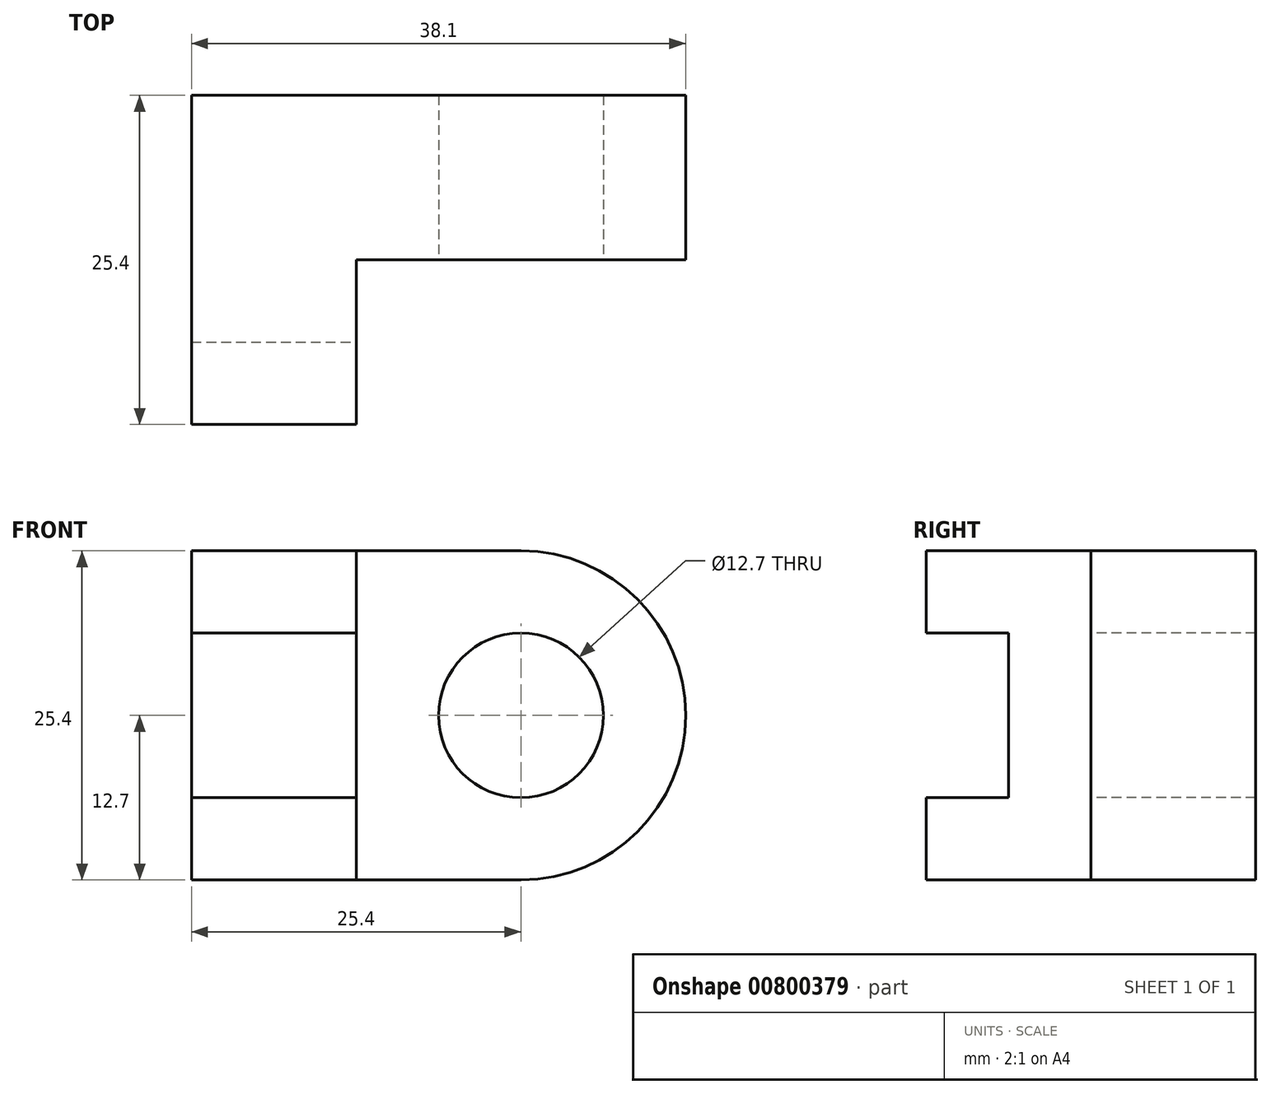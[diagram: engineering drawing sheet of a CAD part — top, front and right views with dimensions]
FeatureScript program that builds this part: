
annotation { "Feature Type Name" : "Feature", "Feature Type Description" : "" }
export const myFeature = defineFeature(function(context is Context, id is Id, definition is map)
    precondition{}
    {
        {
            var Q0;
            Q0=qCreatedBy(makeId("Top.planeOp"),FACE);
            var sketch = newSketch(context, id + "F0", { "sketchPlane" : qUnion([Q0])});
            skLineSegment(sketch, "E0", {"start": v(0, 0) * mm, "end": v(31.75, 0) * mm});
            skLineSegment(sketch, "E1", {"start": v(31.75, 0) * mm, "end": v(31.75, -12.7) * mm});
            skLineSegment(sketch, "E2", {"start": v(31.75, -12.7) * mm, "end": v(12.7, -12.7) * mm});
            skLineSegment(sketch, "E3", {"start": v(12.7, -12.7) * mm, "end": v(12.7, -25.4) * mm});
            skLineSegment(sketch, "E4", {"start": v(12.7, -25.4) * mm, "end": v(0, -25.4) * mm});
            skLineSegment(sketch, "E5", {"start": v(0, -25.4) * mm, "end": v(0, 0) * mm});
            skSolve(sketch);
        }
        {
            var Q0;
            Q0=makeQuery(id+"F0.imprint","IMPRINT",FACE,{"disambiguationData":[TD([[makeQuery(id+"F0.imprint","IMPRINT",EDGE,{"derivedFrom":sQuery(id+"F0.wireOp",EDGE,"E0")}),-1.0]])]});
            extrude(context, id + "F1", {"entities" : qUnion([Q0]), "depth" : 25.4 * mm, "offsetDistance" : 25.4 * mm});
        }
        {
            var Q0;
            Q0=makeQuery(id+"F1.opExtrude","SWEPT_FACE",FACE,{"disambiguationData":[OSD([sQuery(id+"F0.wireOp",EDGE,"E4")])]});
            var sketch = newSketch(context, id + "F2", { "sketchPlane" : qUnion([Q0])});
            skLineSegment(sketch, "E6", {"start": v(0, 19.05) * mm, "end": v(12.7, 19.05) * mm});
            skLineSegment(sketch, "E7", {"start": v(12.7, 19.05) * mm, "end": v(12.7, 6.35) * mm});
            skLineSegment(sketch, "E8", {"start": v(12.7, 6.35) * mm, "end": v(0, 6.35) * mm});
            skLineSegment(sketch, "E9", {"start": v(0, 6.35) * mm, "end": v(0, 19.05) * mm});
            skSolve(sketch);
        }
        {
            var Q0;
            Q0=makeQuery(id+"F2.imprint","IMPRINT",FACE,{"disambiguationData":[TD([[makeQuery(id+"F2.imprint","IMPRINT",EDGE,{"derivedFrom":sQuery(id+"F2.wireOp",EDGE,"E6")}),-1.0]])]});
            extrude(context, id + "F3", {"entities" : qUnion([Q0]), "operationType" : NewBodyOperationType.REMOVE, "oppositeDirection" : true, "depth" : 6.35 * mm, "offsetDistance" : 25.4 * mm});
        }
        {
            var Q0;
            Q0=makeQuery(id+"F1.opExtrude","SWEPT_FACE",FACE,{"disambiguationData":[OSD([sQuery(id+"F0.wireOp",EDGE,"E1")])]});
            extrude(context, id + "F4", {"entities" : qUnion([Q0]), "operationType" : NewBodyOperationType.ADD, "depth" : 6.35 * mm, "offsetDistance" : 25.4 * mm});
        }
        {
            var Q0;
            {var subQ0=sQuery(id+"F0.wireOp",EDGE,"E2");Q0=makeQuery(id+"F4.boolean.opBoolean","MERGE",FACE,{"derivedFrom":[makeQuery(id+"F1.opExtrude","SWEPT_FACE",FACE,{"disambiguationData":[OSD([subQ0])]}),makeQuery(id+"F4.opExtrude","SWEPT_FACE",FACE,{"disambiguationData":[OSD([sQuery(id+"F0.wireOp",EDGE,"E1"),subQ0])]})]});}
            var sketch = newSketch(context, id + "F5", { "sketchPlane" : qUnion([Q0])});
            skLineSegment(sketch, "E10", {"start": v(38.1, 25.4) * mm, "end": v(25.4, 25.4) * mm, "construction": true});
            skLineSegment(sketch, "E11", {"start": v(25.4, 25.4) * mm, "end": v(25.4, 0) * mm, "construction": true});
            skArc(sketch, "E12", {"start": v(25.4, 0) * mm, "mid": v(38.1, 12.7) * mm, "end": v(25.4, 25.4) * mm});
            skSolve(sketch);
        }
        {
            var Q0;
            {var subQ0=sQuery(id+"F5.wireOp",EDGE,"E12");var subQ1=sQuery(id+"F0.wireOp",EDGE,"E2");var subQ2=sQuery(id+"F0.wireOp",EDGE,"E1");var subQ5=makeQuery(id+"F4.opExtrude","CAP_EDGE",EDGE,{"disambiguationData":[OSD([subQ2,subQ1])],"isStart":false});var subQ6=makeQuery(id+"F5.imprint","INTERSECT",VERTEX,{"derivedFrom":[subQ5,subQ0]});Q0=makeQuery(id+"F5.imprint","IMPRINT",FACE,{"disambiguationData":[TD([[makeQuery(id+"F5.imprint","IMPRINT",EDGE,{"disambiguationData":[TD([[subQ6,-1.0]])],"derivedFrom":subQ0}),-1.0]])]});}
            var Q1;
            {var subQ0=sQuery(id+"F5.wireOp",EDGE,"E12");var subQ1=sQuery(id+"F0.wireOp",EDGE,"E2");var subQ2=sQuery(id+"F0.wireOp",EDGE,"E1");var subQ5=makeQuery(id+"F4.opExtrude","CAP_EDGE",EDGE,{"disambiguationData":[OSD([subQ2,subQ1])],"isStart":false});var subQ6=makeQuery(id+"F5.imprint","INTERSECT",VERTEX,{"derivedFrom":[subQ5,subQ0]});Q1=makeQuery(id+"F5.imprint","IMPRINT",FACE,{"disambiguationData":[TD([[makeQuery(id+"F5.imprint","IMPRINT",EDGE,{"disambiguationData":[TD([[subQ6,1.0]])],"derivedFrom":subQ0}),-1.0]])]});}
            extrude(context, id + "F6", {"entities" : qUnion([Q0, Q1]), "operationType" : NewBodyOperationType.REMOVE, "endBound" : BoundingType.THROUGH_ALL, "oppositeDirection" : true, "depth" : 25.4 * mm, "offsetDistance" : 25.4 * mm});
        }
        {
            var Q0;
            {var subQ0=sQuery(id+"F0.wireOp",EDGE,"E2");Q0=makeQuery(id+"F4.boolean.opBoolean","MERGE",FACE,{"derivedFrom":[makeQuery(id+"F1.opExtrude","SWEPT_FACE",FACE,{"disambiguationData":[OSD([subQ0])]}),makeQuery(id+"F4.opExtrude","SWEPT_FACE",FACE,{"disambiguationData":[OSD([sQuery(id+"F0.wireOp",EDGE,"E1"),subQ0])]})]});}
            var sketch = newSketch(context, id + "F7", { "sketchPlane" : qUnion([Q0])});
            skLineSegment(sketch, "E13", {"start": v(38.1, 12.7) * mm, "end": v(25.4, 12.7) * mm, "construction": true});
            skCircle(sketch, "E14", {"center": v(25.4, 12.7) * mm, "radius": 6.35 * mm});
            skSolve(sketch);
        }
        {
            var Q0;
            Q0=makeQuery(id+"F7.imprint","IMPRINT",FACE,{"disambiguationData":[TD([[makeQuery(id+"F7.imprint","IMPRINT",EDGE,{"derivedFrom":sQuery(id+"F7.wireOp",EDGE,"E14")}),1.0]])]});
            extrude(context, id + "F8", {"entities" : qUnion([Q0]), "operationType" : NewBodyOperationType.REMOVE, "endBound" : BoundingType.THROUGH_ALL, "oppositeDirection" : true, "depth" : 25.4 * mm, "offsetDistance" : 25.4 * mm});
        }
    });
